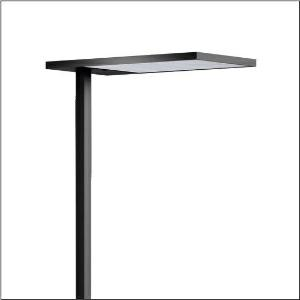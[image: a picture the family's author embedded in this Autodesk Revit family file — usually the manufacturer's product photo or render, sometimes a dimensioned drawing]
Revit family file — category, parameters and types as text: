
# Revit family: silica_21_floor_r_51mx53sg4eb
name_source: partatom
category: Lighting Fixtures
units: mm (PartAtom-declared; Revit-internal decimal feet)

## family parameters
Cut with Voids When Loaded = No
Host = Face
Light Source = No
Part Type = Normal
Room Calculation Point = No
Round Connector Dimension = Use Diameter
Shared = No

## types (1)
- Silica 21 Floor R (1 x LED, 15000 lm, 106.4 W, 4000K)
    Apparent Load = 106 VA
    CIE Flux Codes = 54 86 97 13 100
    Color Rendering = 80
    Color Temperature = 4000K
    Default Elevation = 1800 mm
    Description = Silica® 21 Floor R, floorstanding luminaire, of PMMA, primary optical cover: prismatic diffuser, of PMMA, CAT 2 (L<= 3000cd/m²), light emission: indirect/direct distribution, primary light characteristic: symmetric, primary optical cover: cover panel, of PMMA, installation type: not mounted, LED, rated luminous flux: 15.000lm, luminous efficacy: 141lm/W, light colour: 840, colour temperature: 4000K, control gear: DALI 2, daylight-dependent control, mains connection: 230V, AC, 50/60Hz, connection cable included, cable length: 2,5m, rated input power: 106.4W, luminaire head, of aluminium, powder-coated, jet black (RAL 9005), length: 671mm, width: 371mm, height: 2010mm, supporting column, angular, of aluminium, powder-coated, jet black (RAL 9005), baseplate, of steel, powder-coated, jet black (RAL 9005), sensor module PR3-S, local control - self-sufficient standalone sensors, equipment: master, direct and indirect component separately switchable, protection rating (complete): IP20, insulation class (complete): insulation class I (protective earthing), certification: CE, permissible operating ambient temperature: 0..+35°C, standard: EN 50419, packaging unit: 1 piece
    Height = 18 mm
    Lamp = 1 x LED
    Lamp Light Flux = 15000 lm
    Lamp Power = 106.4 W
    Lamp count = 1
    Length = 650 mm
    Luminous efficacy = 141 lm/W
    Manufacturer = Siteco
    ModVariant = No
    Model = 51MX53SG4EB
    Mounting Place = Floor
    Mounting Type = Freestanding
    Number of Poles = 1
    OnlyDefault = Yes
    Power Factor = 1
    Product Name = Silica 21 Floor R
    Product group = floorstanding luminaire
    ProductGroupID = 1302
    Protection Class = Protection class I
    Protection Degree = IP 20
    RLX_Detail_Level = 1
    RLX_Emergency_Light_Flux = 0 lm
    RLX_Emergency_Type = 0
    RLX_Emergency_Type_DB = No
    RlxData = <blob elided: 22321 chars, md5=2ed0dde4>
    Socket = socket
    Standby Power = 0 W
    System Light Flux = 15000 lm
    System Power = 106 W
    Type Comments = Product without accessories
    Type Image = l_1007011.jpg
    URL = http://relux.com
    VarID = ---
    Voltage = 0 V
    Weight = 0.00 kg
    Width = 350 mm

## geometry (parser evidence)
native form markers: Blend x4, Sweep x15
no freeform markers — native parametric forms only
